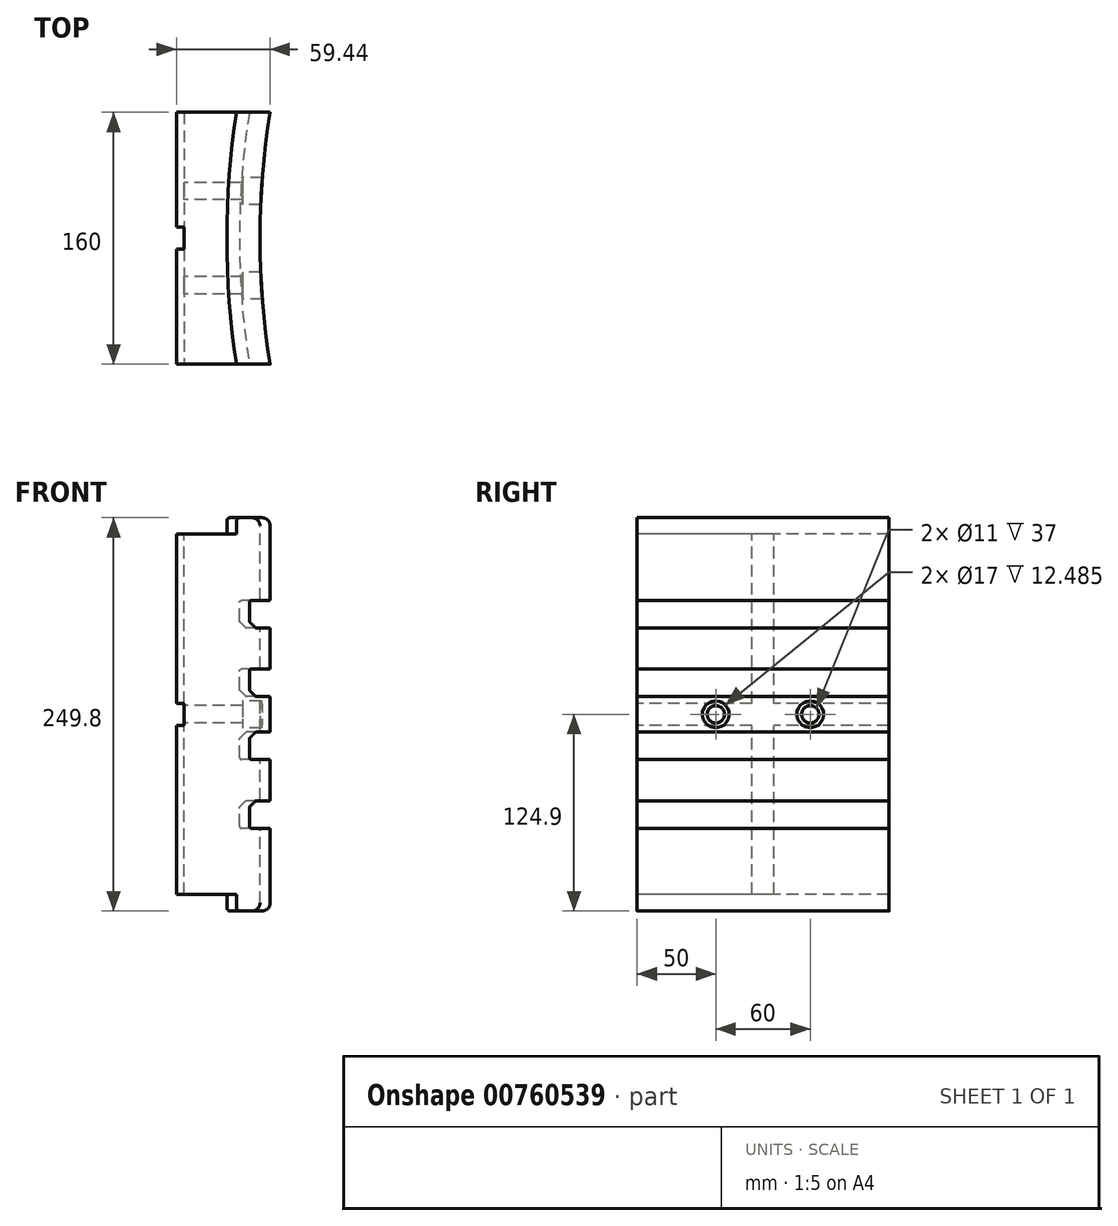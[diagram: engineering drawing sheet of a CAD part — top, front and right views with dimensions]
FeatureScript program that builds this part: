
annotation { "Feature Type Name" : "Feature", "Feature Type Description" : "" }
export const myFeature = defineFeature(function(context is Context, id is Id, definition is map)
    precondition{}
    {
        {
            var Q0;
            Q0=qCreatedBy(makeId("Front.planeOp"),FACE);
            var sketch = newSketch(context, id + "F0", { "sketchPlane" : qUnion([Q0])});
            skLineSegment(sketch, "E0", {"start": v(0, 0) * mm, "end": v(-912, 0) * mm, "construction": true});
            skLineSegment(sketch, "E1", {"start": v(-912, 0) * mm, "end": v(-912, 10.8) * mm});
            skLineSegment(sketch, "E2", {"start": v(-912.5, 11.3) * mm, "end": v(-920.67, 11.3) * mm});
            skLineSegment(sketch, "E3", {"start": v(-921.23, 11.53) * mm, "end": v(-924.41, 14.71) * mm});
            skLineSegment(sketch, "E4", {"start": v(-925, 16.13) * mm, "end": v(-925, 27.3) * mm});
            skLineSegment(sketch, "E5", {"start": v(-923.5, 28.8) * mm, "end": v(-912.5, 28.8) * mm});
            skLineSegment(sketch, "E6", {"start": v(-912, 29.3) * mm, "end": v(-912, 54.4) * mm});
            skLineSegment(sketch, "E7", {"start": v(-912.5, 54.9) * mm, "end": v(-920.67, 54.9) * mm});
            skLineSegment(sketch, "E8", {"start": v(-921.23, 55.13) * mm, "end": v(-924.41, 58.31) * mm});
            skLineSegment(sketch, "E9", {"start": v(-925, 59.73) * mm, "end": v(-925, 70.9) * mm});
            skLineSegment(sketch, "E10", {"start": v(-923.5, 72.4) * mm, "end": v(-912.5, 72.4) * mm});
            skLineSegment(sketch, "E11", {"start": v(-912, 72.9) * mm, "end": v(-912, 119.9) * mm});
            skLineSegment(sketch, "E12", {"start": v(-917, 124.9) * mm, "end": v(-931, 124.9) * mm});
            skLineSegment(sketch, "E13", {"start": v(-933, 122.9) * mm, "end": v(-933, 115.2) * mm});
            skLineSegment(sketch, "E14", {"start": v(-933.8, 114.4) * mm, "end": v(-965, 114.4) * mm});
            skLineSegment(sketch, "E15", {"start": v(-965, 114.4) * mm, "end": v(-965, 0) * mm});
            skLineSegment(sketch, "E16", {"start": v(-412, 128.8) * mm, "end": v(-412, -136.8) * mm, "construction": true});
            skPoint(sketch, "E17.visualSharp", {"position": v(-912, 124.9) * mm});
            skArc(sketch, "E17.filletArc", {"start": v(-912, 119.9) * mm, "mid": v(-913.46, 123.44) * mm, "end": v(-917, 124.9) * mm});
            skPoint(sketch, "E18.visualSharp", {"position": v(-912, 54.9) * mm});
            skArc(sketch, "E18.filletArc", {"start": v(-912, 54.4) * mm, "mid": v(-912.15, 54.75) * mm, "end": v(-912.5, 54.9) * mm});
            skPoint(sketch, "E19.visualSharp", {"position": v(-912, 28.8) * mm});
            skArc(sketch, "E19.filletArc", {"start": v(-912.5, 28.8) * mm, "mid": v(-912.15, 28.95) * mm, "end": v(-912, 29.3) * mm});
            skPoint(sketch, "E20.visualSharp", {"position": v(-912, 11.3) * mm});
            skArc(sketch, "E20.filletArc", {"start": v(-912, 10.8) * mm, "mid": v(-912.15, 11.15) * mm, "end": v(-912.5, 11.3) * mm});
            skPoint(sketch, "E21.visualSharp", {"position": v(-925, 72.4) * mm});
            skArc(sketch, "E21.filletArc", {"start": v(-923.5, 72.4) * mm, "mid": v(-924.56, 71.96) * mm, "end": v(-925, 70.9) * mm});
            skPoint(sketch, "E22.visualSharp", {"position": v(-925, 28.8) * mm});
            skArc(sketch, "E22.filletArc", {"start": v(-923.5, 28.8) * mm, "mid": v(-924.56, 28.36) * mm, "end": v(-925, 27.3) * mm});
            skPoint(sketch, "E23.visualSharp", {"position": v(-925, 15.3) * mm});
            skArc(sketch, "E23.filletArc", {"start": v(-925, 16.13) * mm, "mid": v(-924.85, 15.36) * mm, "end": v(-924.41, 14.71) * mm});
            skPoint(sketch, "E24.visualSharp", {"position": v(-925, 58.9) * mm});
            skArc(sketch, "E24.filletArc", {"start": v(-925, 59.73) * mm, "mid": v(-924.85, 58.96) * mm, "end": v(-924.41, 58.31) * mm});
            skPoint(sketch, "E25.visualSharp", {"position": v(-921, 11.3) * mm});
            skArc(sketch, "E25.filletArc", {"start": v(-921.23, 11.53) * mm, "mid": v(-920.97, 11.36) * mm, "end": v(-920.67, 11.3) * mm});
            skPoint(sketch, "E26.visualSharp", {"position": v(-921, 54.9) * mm});
            skArc(sketch, "E26.filletArc", {"start": v(-921.23, 55.13) * mm, "mid": v(-920.97, 54.96) * mm, "end": v(-920.67, 54.9) * mm});
            skPoint(sketch, "E27.visualSharp", {"position": v(-912, 72.4) * mm});
            skArc(sketch, "E27.filletArc", {"start": v(-912.5, 72.4) * mm, "mid": v(-912.15, 72.55) * mm, "end": v(-912, 72.9) * mm});
            skPoint(sketch, "E28.visualSharp", {"position": v(-933, 114.4) * mm});
            skArc(sketch, "E28.filletArc", {"start": v(-933.8, 114.4) * mm, "mid": v(-933.23, 114.63) * mm, "end": v(-933, 115.2) * mm});
            skPoint(sketch, "E29.visualSharp", {"position": v(-933, 124.9) * mm});
            skArc(sketch, "E29.filletArc", {"start": v(-931, 124.9) * mm, "mid": v(-932.41, 124.31) * mm, "end": v(-933, 122.9) * mm});
            skArc(sketch, "E30.MirrorCS", {"start": v(-921.23, -11.53) * mm, "mid": v(-920.97, -11.36) * mm, "end": v(-920.67, -11.3) * mm});
            skArc(sketch, "E31.MirrorCS", {"start": v(-912.5, -72.4) * mm, "mid": v(-912.15, -72.55) * mm, "end": v(-912, -72.9) * mm});
            skArc(sketch, "E32.MirrorCS", {"start": v(-923.5, -72.4) * mm, "mid": v(-924.56, -71.96) * mm, "end": v(-925, -70.9) * mm});
            skArc(sketch, "E33.MirrorCS", {"start": v(-923.5, -28.8) * mm, "mid": v(-924.56, -28.36) * mm, "end": v(-925, -27.3) * mm});
            skLineSegment(sketch, "E34.MirrorCS", {"start": v(-923.5, -72.4) * mm, "end": v(-912.5, -72.4) * mm});
            skLineSegment(sketch, "E35.MirrorCS", {"start": v(-925, -16.13) * mm, "end": v(-925, -27.3) * mm});
            skLineSegment(sketch, "E36.MirrorCS", {"start": v(-921.23, -11.53) * mm, "end": v(-924.41, -14.71) * mm});
            skLineSegment(sketch, "E37.MirrorCS", {"start": v(-912.5, -11.3) * mm, "end": v(-920.67, -11.3) * mm});
            skArc(sketch, "E38.MirrorCS", {"start": v(-912, -54.4) * mm, "mid": v(-912.15, -54.75) * mm, "end": v(-912.5, -54.9) * mm});
            skArc(sketch, "E39.MirrorCS", {"start": v(-912, -10.8) * mm, "mid": v(-912.15, -11.15) * mm, "end": v(-912.5, -11.3) * mm});
            skArc(sketch, "E40.MirrorCS", {"start": v(-925, -16.13) * mm, "mid": v(-924.85, -15.36) * mm, "end": v(-924.41, -14.71) * mm});
            skLineSegment(sketch, "E41.MirrorCS", {"start": v(-912, 0) * mm, "end": v(-912, -10.8) * mm});
            skArc(sketch, "E42.MirrorCS", {"start": v(-925, -59.73) * mm, "mid": v(-924.85, -58.96) * mm, "end": v(-924.41, -58.31) * mm});
            skArc(sketch, "E43.MirrorCS", {"start": v(-921.23, -55.13) * mm, "mid": v(-920.97, -54.96) * mm, "end": v(-920.67, -54.9) * mm});
            skLineSegment(sketch, "E44.MirrorCS", {"start": v(-921.23, -55.13) * mm, "end": v(-924.41, -58.31) * mm});
            skLineSegment(sketch, "E45.MirrorCS", {"start": v(-912.5, -54.9) * mm, "end": v(-920.67, -54.9) * mm});
            skArc(sketch, "E46.MirrorCS", {"start": v(-912.5, -28.8) * mm, "mid": v(-912.15, -28.95) * mm, "end": v(-912, -29.3) * mm});
            skLineSegment(sketch, "E47.MirrorCS", {"start": v(-925, -59.73) * mm, "end": v(-925, -70.9) * mm});
            skLineSegment(sketch, "E48.MirrorCS", {"start": v(-923.5, -28.8) * mm, "end": v(-912.5, -28.8) * mm});
            skArc(sketch, "E49.MirrorCS", {"start": v(-933.8, -114.4) * mm, "mid": v(-933.23, -114.63) * mm, "end": v(-933, -115.2) * mm});
            skLineSegment(sketch, "E50.MirrorCS", {"start": v(-933, -122.9) * mm, "end": v(-933, -115.2) * mm});
            skArc(sketch, "E51.MirrorCS", {"start": v(-931, -124.9) * mm, "mid": v(-932.41, -124.31) * mm, "end": v(-933, -122.9) * mm});
            skArc(sketch, "E52.MirrorCS", {"start": v(-912, -119.9) * mm, "mid": v(-913.46, -123.44) * mm, "end": v(-917, -124.9) * mm});
            skLineSegment(sketch, "E53.MirrorCS", {"start": v(-917, -124.9) * mm, "end": v(-931, -124.9) * mm});
            skPoint(sketch, "E54.MirrorP", {"position": v(-925, -58.9) * mm});
            skPoint(sketch, "E55.MirrorP", {"position": v(-925, -15.3) * mm});
            skPoint(sketch, "E56.MirrorP", {"position": v(-921, -11.3) * mm});
            skPoint(sketch, "E57.MirrorP", {"position": v(-921, -54.9) * mm});
            skLineSegment(sketch, "E58.MirrorCS", {"start": v(-912, -72.9) * mm, "end": v(-912, -119.9) * mm});
            skLineSegment(sketch, "E59.MirrorCS", {"start": v(-912, -29.3) * mm, "end": v(-912, -54.4) * mm});
            skPoint(sketch, "E60.MirrorP", {"position": v(-912, -54.9) * mm});
            skPoint(sketch, "E61.MirrorP", {"position": v(-912, -72.4) * mm});
            skPoint(sketch, "E62.MirrorP", {"position": v(-912, -28.8) * mm});
            skLineSegment(sketch, "E63.MirrorCS", {"start": v(-965, -114.4) * mm, "end": v(-965, 0) * mm});
            skLineSegment(sketch, "E64.MirrorCS", {"start": v(-933.8, -114.4) * mm, "end": v(-965, -114.4) * mm});
            skPoint(sketch, "E65.MirrorP", {"position": v(-933, -114.4) * mm});
            skPoint(sketch, "E66.MirrorP", {"position": v(-925, -28.8) * mm});
            skPoint(sketch, "E67.MirrorP", {"position": v(-925, -72.4) * mm});
            skPoint(sketch, "E68.MirrorP", {"position": v(-912, -11.3) * mm});
            skPoint(sketch, "E69.MirrorP", {"position": v(-933, -124.9) * mm});
            skPoint(sketch, "E70.MirrorP", {"position": v(-912, -124.9) * mm});
            skSolve(sketch);
        }
        {
            var Q0;
            Q0=qCreatedBy(makeId("Top.planeOp"),FACE);
            var sketch = newSketch(context, id + "F1", { "sketchPlane" : qUnion([Q0])});
            skArc(sketch, "E71", {"start": v(-905.56, 80) * mm, "mid": v(-912, 0) * mm, "end": v(-905.56, -80) * mm});
            skLineSegment(sketch, "E72", {"start": v(-965, 80) * mm, "end": v(-965, 0) * mm, "construction": true});
            skLineSegment(sketch, "E73", {"start": v(-965, 80) * mm, "end": v(-905.56, 80) * mm, "construction": true});
            skLineSegment(sketch, "E74", {"start": v(-905.56, 80) * mm, "end": v(-412, 0) * mm, "construction": true});
            skLineSegment(sketch, "E75.MirrorCS", {"start": v(-905.56, -80) * mm, "end": v(-412, 0) * mm, "construction": true});
            skLineSegment(sketch, "E76.MirrorCS", {"start": v(-965, -80) * mm, "end": v(-965, 0) * mm, "construction": true});
            skLineSegment(sketch, "E77.MirrorCS", {"start": v(-965, -80) * mm, "end": v(-905.56, -80) * mm, "construction": true});
            skPoint(sketch, "E78.orphan", {"position": v(-765.93, 80) * mm});
            skPoint(sketch, "E79.orphan", {"position": v(-765.93, -80) * mm});
            skSolve(sketch);
        }
        {
            var Q0;
            Q0=qSketchRegion(id+"F0",true);
            var Q1;
            Q1=sQuery(id+"F1.wireOp",EDGE,"E71");
            sweep(context, id + "F2", {"profiles" : qUnion([Q0]), "path" : qUnion([Q1])});
        }
        {
            var Q0;
            Q0=makeQuery(id+"F2.opSweep","SWEPT_FACE",FACE,{"disambiguationData":[OSD([sQuery(id+"F0.wireOp",EDGE,"E12"),sQuery(id+"F1.wireOp",EDGE,"E71")])]});
            var sketch = newSketch(context, id + "F3", { "sketchPlane" : qUnion([Q0])});
            skCircle(sketch, "E80", {"center": v(-412, 0) * mm, "radius": 500 * mm, "construction": true});
            skLineSegment(sketch, "E81", {"start": v(-959.18, 80) * mm, "end": v(-905.56, 80) * mm});
            skLineSegment(sketch, "E82", {"start": v(-412, 0) * mm, "end": v(-965, 0) * mm, "construction": true});
            skLineSegment(sketch, "E83", {"start": v(-957.88, 88.48) * mm, "end": v(-905.56, 80) * mm});
            skArc(sketch, "E84", {"start": v(-957.88, 88.48) * mm, "mid": v(-958.55, 84.24) * mm, "end": v(-959.18, 80) * mm});
            skLineSegment(sketch, "E85.MirrorCS", {"start": v(-957.88, -88.48) * mm, "end": v(-905.56, -80) * mm});
            skArc(sketch, "E86.MirrorCS", {"start": v(-957.88, -88.48) * mm, "mid": v(-958.55, -84.24) * mm, "end": v(-959.18, -80) * mm});
            skLineSegment(sketch, "E87.MirrorCS", {"start": v(-959.18, -80) * mm, "end": v(-905.56, -80) * mm});
            skSolve(sketch);
        }
        {
            var Q0;
            Q0=qSketchRegion(id+"F3",true);
            extrude(context, id + "F4", {"entities" : qUnion([Q0]), "operationType" : NewBodyOperationType.REMOVE, "endBound" : BoundingType.THROUGH_ALL, "oppositeDirection" : true, "depth" : 25 * mm, "offsetDistance" : 25 * mm});
        }
        {
            var Q0;
            Q0=makeQuery(id+"F2.opSweep","SWEPT_FACE",FACE,{"disambiguationData":[OSD([sQuery(id+"F0.wireOp",EDGE,"E14"),sQuery(id+"F1.wireOp",EDGE,"E71")])]});
            var sketch = newSketch(context, id + "F5", { "sketchPlane" : qUnion([Q0])});
            skLineSegment(sketch, "E88", {"start": v(-959.18, 80) * mm, "end": v(-965, 80) * mm});
            skLineSegment(sketch, "E89", {"start": v(-965, 80) * mm, "end": v(-965, -80) * mm});
            skLineSegment(sketch, "E90", {"start": v(-965, -80) * mm, "end": v(-959.18, -80) * mm});
            skArc(sketch, "E91", {"start": v(-959.18, 80) * mm, "mid": v(-965, 0) * mm, "end": v(-959.18, -80) * mm});
            skSolve(sketch);
        }
        {
            var Q0;
            {var subQ0=sQuery(id+"F5.wireOp",EDGE,"E90");Q0=makeQuery(id+"F5.imprint","IMPRINT",FACE,{"disambiguationData":[TD([[makeQuery(id+"F5.imprint","IMPRINT",EDGE,{"derivedFrom":subQ0}),1.0]])]});}
            var Q1;
            {var subQ0=sQuery(id+"F5.wireOp",EDGE,"E88");Q1=makeQuery(id+"F5.imprint","IMPRINT",FACE,{"disambiguationData":[TD([[makeQuery(id+"F5.imprint","IMPRINT",EDGE,{"derivedFrom":subQ0}),1.0]])]});}
            var Q2;
            Q2=makeQuery(id+"F2.opSweep","SWEPT_FACE",FACE,{"disambiguationData":[OSD([sQuery(id+"F0.wireOp",EDGE,"E64.MirrorCS"),sQuery(id+"F1.wireOp",EDGE,"E71")])]});
            extrude(context, id + "F6", {"entities" : qUnion([Q0, Q1]), "operationType" : NewBodyOperationType.ADD, "endBound" : BoundingType.UP_TO_SURFACE, "oppositeDirection" : true, "depth" : 25 * mm, "endBoundEntityFace" : qUnion([Q2]), "offsetDistance" : 25 * mm});
        }
        {
            var Q0;
            {var subQ0=sQuery(id+"F5.wireOp",EDGE,"E89");Q0=makeQuery(id+"F6.boolean.opBoolean","MERGE",FACE,{"derivedFrom":[makeQuery(id+"F6.opExtrude","SWEPT_FACE",FACE,{"disambiguationData":[OSD([subQ0]),TDD([makeQuery(id+"F5.imprint","IMPRINT",EDGE,{"disambiguationData":[TD([[makeQuery(id+"F5.imprint","INTERSECT",VERTEX,{"derivedFrom":[sQuery(id+"F5.wireOp",EDGE,"E88"),subQ0]}),-1.0]])],"derivedFrom":subQ0})])]}),makeQuery(id+"F6.opExtrude","SWEPT_FACE",FACE,{"disambiguationData":[OSD([subQ0]),TDD([makeQuery(id+"F5.imprint","IMPRINT",EDGE,{"disambiguationData":[TD([[makeQuery(id+"F5.imprint","INTERSECT",VERTEX,{"derivedFrom":[subQ0,sQuery(id+"F5.wireOp",EDGE,"E90")]}),1.0]])],"derivedFrom":subQ0})])]})]});}
            var sketch = newSketch(context, id + "F7", { "sketchPlane" : qUnion([Q0])});
            skLineSegment(sketch, "E92.bottom", {"start": v(-7, -114.4) * mm, "end": v(7, -114.4) * mm});
            skLineSegment(sketch, "E92.top", {"start": v(-7, 114.4) * mm, "end": v(7, 114.4) * mm});
            skLineSegment(sketch, "E92.left", {"start": v(-7, -114.4) * mm, "end": v(-7, -7) * mm});
            skLineSegment(sketch, "E92.right", {"start": v(7, -114.4) * mm, "end": v(7, -7) * mm});
            skLineSegment(sketch, "E93.bottom", {"start": v(-80, -7) * mm, "end": v(-7, -7) * mm});
            skLineSegment(sketch, "E93.top", {"start": v(-80, 7) * mm, "end": v(-7, 7) * mm});
            skLineSegment(sketch, "E93.left", {"start": v(-80, -7) * mm, "end": v(-80, 7) * mm});
            skLineSegment(sketch, "E93.right", {"start": v(80, -7) * mm, "end": v(80, 7) * mm});
            skLineSegment(sketch, "E94.trimOffspring", {"start": v(-7, 7) * mm, "end": v(-7, 114.4) * mm});
            skLineSegment(sketch, "E95.trimOffspring", {"start": v(7, 7) * mm, "end": v(80, 7) * mm});
            skLineSegment(sketch, "E96.trimOffspring", {"start": v(7, 7) * mm, "end": v(7, 114.4) * mm});
            skLineSegment(sketch, "E97.trimOffspring", {"start": v(7, -7) * mm, "end": v(80, -7) * mm});
            skSolve(sketch);
        }
        {
            var Q0;
            Q0=qSketchRegion(id+"F7",true);
            extrude(context, id + "F8", {"entities" : qUnion([Q0]), "operationType" : NewBodyOperationType.REMOVE, "oppositeDirection" : true, "depth" : 5 * mm, "offsetDistance" : 25 * mm});
        }
        {
            var Q0;
            Q0=makeQuery(id+"F8.boolean.opBoolean","COPY",FACE,{"derivedFrom":makeQuery(id+"F8.opExtrude","CAP_FACE",FACE,{"disambiguationData":[OSD([sQuery(id+"F7.wireOp",EDGE,"E92.bottom"),sQuery(id+"F7.wireOp",EDGE,"E92.top"),sQuery(id+"F7.wireOp",EDGE,"E92.left"),sQuery(id+"F7.wireOp",EDGE,"E92.right"),sQuery(id+"F7.wireOp",EDGE,"E93.bottom"),sQuery(id+"F7.wireOp",EDGE,"E93.top"),sQuery(id+"F7.wireOp",EDGE,"E93.left"),sQuery(id+"F7.wireOp",EDGE,"E93.right"),sQuery(id+"F7.wireOp",EDGE,"E94.trimOffspring"),sQuery(id+"F7.wireOp",EDGE,"E95.trimOffspring"),sQuery(id+"F7.wireOp",EDGE,"E96.trimOffspring"),sQuery(id+"F7.wireOp",EDGE,"E97.trimOffspring")])],"isStart":false})});
            var sketch = newSketch(context, id + "F9", { "sketchPlane" : qUnion([Q0])});
            skCircle(sketch, "E98", {"center": v(-30, 0) * mm, "radius": 5.5 * mm});
            skCircle(sketch, "E99", {"center": v(30, 0) * mm, "radius": 5.5 * mm});
            skSolve(sketch);
        }
        {
            var Q0;
            Q0=qSketchRegion(id+"F9",true);
            extrude(context, id + "F10", {"entities" : qUnion([Q0]), "operationType" : NewBodyOperationType.REMOVE, "endBound" : BoundingType.UP_TO_NEXT, "oppositeDirection" : true, "depth" : 25 * mm, "offsetDistance" : 25 * mm});
        }
        {
            var Q0;
            {var subQ0=sQuery(id+"F5.wireOp",EDGE,"E91");var subQ1=sQuery(id+"F5.wireOp",EDGE,"E89");Q0=makeQuery(id+"F6.boolean.opBoolean","MERGE",FACE,{"derivedFrom":[makeQuery(id+"F2.opSweep","SWEPT_FACE",FACE,{"disambiguationData":[OSD([sQuery(id+"F0.wireOp",EDGE,"E14"),sQuery(id+"F1.wireOp",EDGE,"E71")])]}),makeQuery(id+"F6.opExtrude","CAP_FACE",FACE,{"disambiguationData":[OSD([sQuery(id+"F5.wireOp",EDGE,"E88"),subQ1,subQ0])],"isStart":true}),makeQuery(id+"F6.opExtrude","CAP_FACE",FACE,{"disambiguationData":[OSD([subQ1,sQuery(id+"F5.wireOp",EDGE,"E90"),subQ0])],"isStart":true})]});}
            var sketch = newSketch(context, id + "F11", { "sketchPlane" : qUnion([Q0])});
            skLineSegment(sketch, "E100", {"start": v(-412, 0) * mm, "end": v(-965, 0) * mm, "construction": true});
            skPoint(sketch, "E100.endSnap0", {"position": v(-960, 0) * mm});
            skLineSegment(sketch, "E101", {"start": v(-912, 147.31) * mm, "end": v(-912, -195.98) * mm, "construction": true});
            skLineSegment(sketch, "E102", {"start": v(-923, 147.31) * mm, "end": v(-923, -195.98) * mm, "construction": true});
            skSolve(sketch);
        }
        {
            var Q0;
            {var subQ0=sQuery(id+"F1.wireOp",EDGE,"E71");var subQ1=sQuery(id+"F0.wireOp",EDGE,"E64.MirrorCS");Q0=makeQuery(id+"F6.boolean.opBoolean","MERGE",FACE,{"derivedFrom":[makeQuery(id+"F2.opSweep","SWEPT_FACE",FACE,{"disambiguationData":[OSD([subQ1,subQ0])]}),makeQuery(id+"F6.opExtrude","CAP_FACE",FACE,{"disambiguationData":[OSD([subQ1,subQ0]),OD(0.0)],"isStart":false}),makeQuery(id+"F6.opExtrude","CAP_FACE",FACE,{"disambiguationData":[OSD([subQ1,subQ0]),OD(1.0)],"isStart":false})]});}
            var sketch = newSketch(context, id + "F12", { "sketchPlane" : qUnion([Q0])});
            skLineSegment(sketch, "E103", {"start": v(-912, 194.28) * mm, "end": v(-912, -106.74) * mm, "construction": true});
            skLineSegment(sketch, "E104", {"start": v(-923, 195.68) * mm, "end": v(-923, -104.26) * mm, "construction": true});
            skSolve(sketch);
        }
        {
            var Q0;
            Q0=sQuery(id+"F11.wireOp",VERTEX,"E102.end");
            var Q1;
            Q1=sQuery(id+"F12.wireOp",VERTEX,"E104.start");
            var Q2;
            Q2=sQuery(id+"F11.wireOp",VERTEX,"E102.start");
            cPlane(context, id + "F13", {"entities" : qUnion([Q0, Q1, Q2]), "cplaneType" : CPlaneType.THREE_POINT, "offset" : 25 * mm, "width" : 150 * mm, "height" : 150 * mm});
        }
        {
            var Q0;
            Q0=qCreatedBy(id+"F13.planeOp",FACE);
            var sketch = newSketch(context, id + "F14", { "sketchPlane" : qUnion([Q0])});
            skCircle(sketch, "E105", {"center": v(30, 0) * mm, "radius": 8.5 * mm});
            skCircle(sketch, "E106", {"center": v(-30, 0) * mm, "radius": 8.5 * mm});
            skSolve(sketch);
        }
        {
            var Q0;
            Q0=qSketchRegion(id+"F14",true);
            extrude(context, id + "F15", {"entities" : qUnion([Q0]), "operationType" : NewBodyOperationType.REMOVE, "oppositeDirection" : true, "depth" : 25 * mm, "offsetDistance" : 25 * mm});
        }
    });
